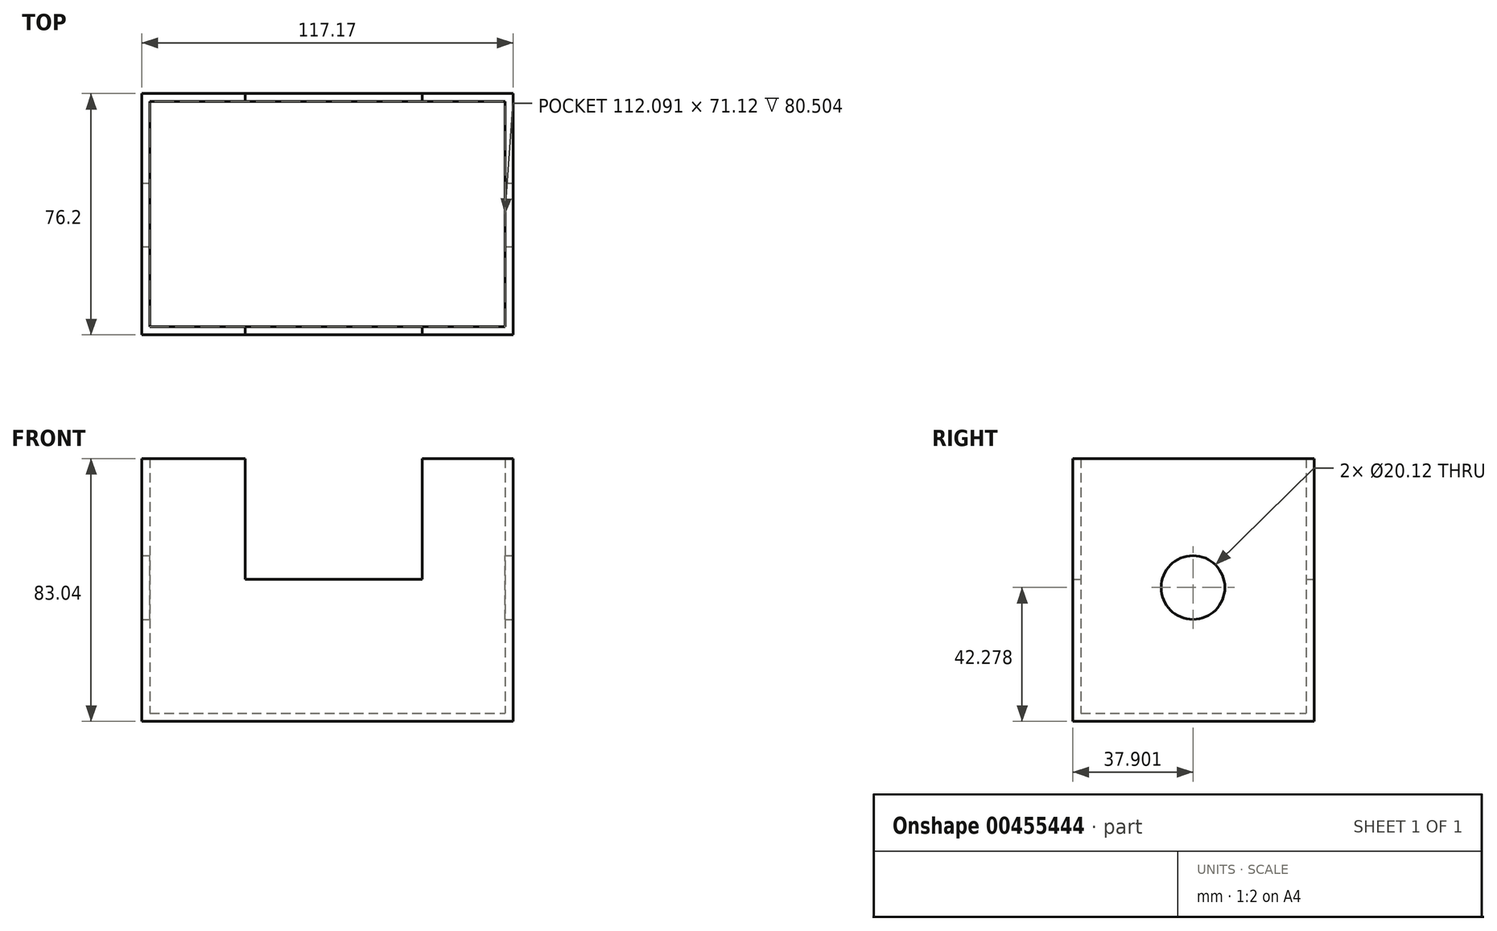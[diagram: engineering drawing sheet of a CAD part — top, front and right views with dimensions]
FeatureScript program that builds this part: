
annotation { "Feature Type Name" : "Feature", "Feature Type Description" : "" }
export const myFeature = defineFeature(function(context is Context, id is Id, definition is map)
    precondition{}
    {
        {
            var Q0;
            Q0=qCreatedBy(makeId("Front.planeOp"),FACE);
            var sketch = newSketch(context, id + "F0", { "sketchPlane" : qUnion([Q0])});
            skLineSegment(sketch, "E0.bottom", {"start": v(-53.47, 51.2) * mm, "end": v(63.7, 51.2) * mm});
            skLineSegment(sketch, "E0.top", {"start": v(-53.47, -31.85) * mm, "end": v(63.7, -31.85) * mm});
            skLineSegment(sketch, "E0.left", {"start": v(-53.47, 51.2) * mm, "end": v(-53.47, -31.85) * mm});
            skLineSegment(sketch, "E0.right", {"start": v(63.7, 51.2) * mm, "end": v(63.7, -31.85) * mm});
            skLineSegment(sketch, "E1.bottom", {"start": v(-20.88, 51.2) * mm, "end": v(34.95, 51.2) * mm});
            skLineSegment(sketch, "E1.top", {"start": v(-20.88, 13) * mm, "end": v(34.95, 13) * mm});
            skLineSegment(sketch, "E1.left", {"start": v(-20.88, 51.2) * mm, "end": v(-20.88, 13) * mm});
            skLineSegment(sketch, "E1.right", {"start": v(34.95, 51.2) * mm, "end": v(34.95, 13) * mm});
            skSolve(sketch);
        }
        {
            var Q0;
            Q0=makeQuery(id+"F0.imprint","IMPRINT",FACE,{"disambiguationData":[TD([[makeQuery(id+"F0.imprint","IMPRINT",EDGE,{"derivedFrom":sQuery(id+"F0.wireOp",EDGE,"E0.top")}),1.0]])]});
            extrude(context, id + "F1", {"entities" : qUnion([Q0]), "depth" : 76.2 * mm});
        }
        {
            var Q0;
            Q0=makeQuery(id+"F1.opExtrude","SWEPT_FACE",FACE,{"disambiguationData":[OSD([sQuery(id+"F0.wireOp",EDGE,"E0.bottom")])]});
            var Q1;
            Q1=makeQuery(id+"F1.opExtrude","SWEPT_FACE",FACE,{"disambiguationData":[OSD([sQuery(id+"F0.wireOp",EDGE,"E1.left")])]});
            var Q2;
            Q2=makeQuery(id+"F1.opExtrude","SWEPT_FACE",FACE,{"disambiguationData":[OSD([sQuery(id+"F0.wireOp",EDGE,"E1.top")])]});
            var Q3;
            Q3=makeQuery(id+"F1.opExtrude","SWEPT_FACE",FACE,{"disambiguationData":[OSD([sQuery(id+"F0.wireOp",EDGE,"E1.right")])]});
            shell(context, id + "F2", {"entities" : qUnion([Q0, Q1, Q2, Q3]), "thickness" : 2.54 * mm});
        }
        {
            var Q0;
            Q0=makeQuery(id+"F1.opExtrude","SWEPT_FACE",FACE,{"disambiguationData":[OSD([sQuery(id+"F0.wireOp",EDGE,"E0.right")])]});
            var sketch = newSketch(context, id + "F3", { "sketchPlane" : qUnion([Q0])});
            skCircle(sketch, "E2", {"center": v(-38.3, 10.43) * mm, "radius": 10.06 * mm});
            skSolve(sketch);
        }
        {
            var Q0;
            Q0 = qSketchRegion(id + "F3", true);
            extrude(context, id + "F4", {"entities" : qUnion([Q0]), "operationType" : NewBodyOperationType.REMOVE, "endBound" : BoundingType.THROUGH_ALL, "oppositeDirection" : true, "depth" : 25.4 * mm});
        }
    });
